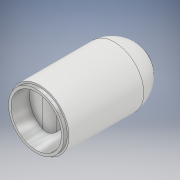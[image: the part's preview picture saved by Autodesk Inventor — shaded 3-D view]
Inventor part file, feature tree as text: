
AUTODESK INVENTOR PART (.ipt)
format: ipt  version: 2018 (Build 220112000, 112)  size: 184,832 bytes
history: native  units: in
note: dims shown in document units (in); Inventor stores cm internally (conversion verified against a paired STEP export)
features: sketch x2, revolve x1, extrude x1, fillet x1
ambient origin geometry x8: Origin, YZ Plane, XZ Plane, XY Plane, X Axis, Y Axis, Z Axis, Center Point
bodies: Solid1 (feature_tree)
feature tree (5):
  revolve  "Revolution1"  [1 undecoded]
  extrude  "Extrusion1"  Depth=0.04in
  fillet  "Fillet1"  Radius=0.01in
  sketch  "Sketch1"  dims[d0=0.64in d2=0.175in]
  sketch  "Sketch2"  dims[d3=0.11in d4=0.02in d5=0.01in d7=0.015in d8=90.0deg d9=0.03in d10=0.03in d11=0.35in d12=0.0in d13=0.04in]
note: 1 required parameter value undecoded (feature->parameter linkage not recoverable at this tier; creation-order binding heuristic only, values carry confidence <= 0.55)
